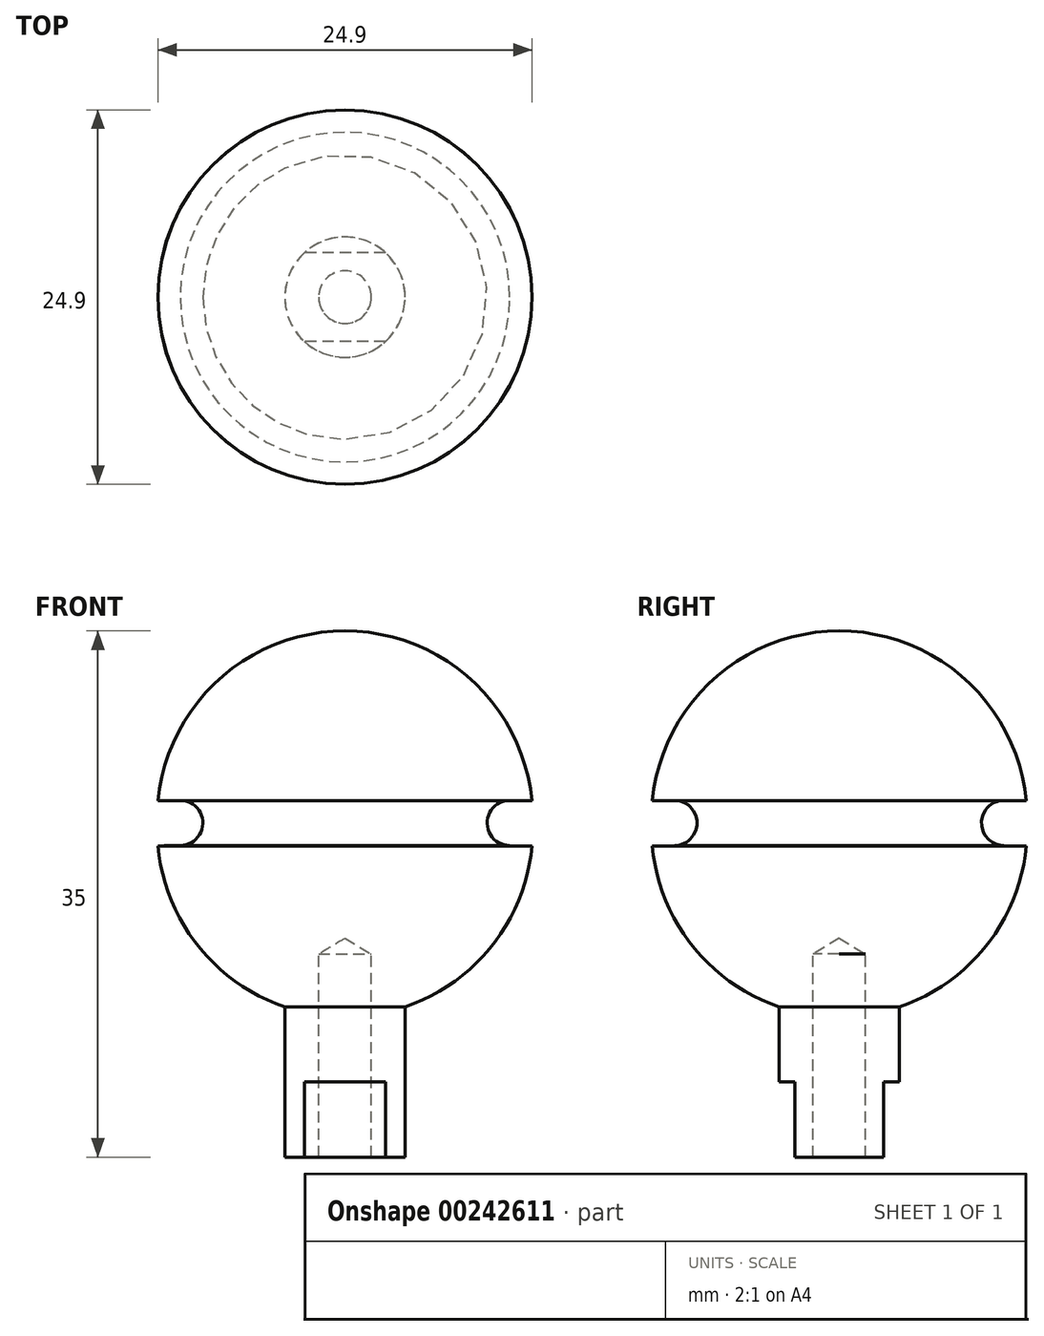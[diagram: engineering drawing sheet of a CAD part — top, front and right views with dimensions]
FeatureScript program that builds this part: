
annotation { "Feature Type Name" : "Feature", "Feature Type Description" : "" }
export const myFeature = defineFeature(function(context is Context, id is Id, definition is map)
    precondition{}
    {
        {
            var Q0;
            Q0=qCreatedBy(makeId("Top.planeOp"),FACE);
            var sketch = newSketch(context, id + "F0", { "sketchPlane" : qUnion([Q0])});
            skPoint(sketch, "E0", {"position": v(0, 0) * mm});
            skCircle(sketch, "E1", {"center": v(0, 0) * mm, "radius": 4 * mm});
            skSolve(sketch);
        }
        {
            var Q0;
            Q0=makeQuery(id+"F0.imprint","IMPRINT",FACE,{"disambiguationData":[TD([[makeQuery(id+"F0.imprint","IMPRINT",EDGE,{"derivedFrom":sQuery(id+"F0.wireOp",EDGE,"E1")}),1.0]])]});
            extrude(context, id + "F1", {"entities" : qUnion([Q0]), "offsetDistance" : 25 * mm, "depth" : 10 * mm});
        }
        {
            var Q0;
            Q0=makeQuery(id+"F1.opExtrude","CAP_FACE",FACE,{"disambiguationData":[OSD([sQuery(id+"F0.wireOp",EDGE,"E1")])],"isStart":false});
            var sketch = newSketch(context, id + "F2", { "sketchPlane" : qUnion([Q0])});
            skCircle(sketch, "E2", {"center": v(0, 0) * mm, "radius": 12.5 * mm});
            skSolve(sketch);
        }
        {
            var Q0;
            Q0 = qSketchRegion(id + "F2", true);
            extrude(context, id + "F3", {"entities" : qUnion([Q0]), "operationType" : NewBodyOperationType.ADD, "depth" : 25 * mm, "offsetDistance" : 25 * mm});
        }
        {
            var Q0;
            Q0=makeQuery(id+"F3.opExtrude","CAP_EDGE",EDGE,{"disambiguationData":[OSD([sQuery(id+"F2.wireOp",EDGE,"E2")])],"isStart":false});
            var Q1;
            Q1=makeQuery(id+"F3.opExtrude","CAP_EDGE",EDGE,{"disambiguationData":[OSD([sQuery(id+"F2.wireOp",EDGE,"E2")])],"isStart":true});
            fillet(context, id + "F4", {"entities" : qUnion([Q0, Q1]), "radius" : 12.5 * mm, "tangentPropagation" : true, "allowEdgeOverflow" : false});
        }
        {
            var Q0;
            Q0=qCreatedBy(makeId("Right.planeOp"),FACE);
            var sketch = newSketch(context, id + "F5", { "sketchPlane" : qUnion([Q0])});
            skLineSegment(sketch, "E3", {"start": v(12.5, 23.7) * mm, "end": v(12.5, 20.7) * mm, "construction": true});
            skPoint(sketch, "E4", {"position": v(12.5, 22.2) * mm});
            skLineSegment(sketch, "E5", {"start": v(10.96, 23.73) * mm, "end": v(10.96, 20.73) * mm, "construction": true});
            skPoint(sketch, "E6", {"position": v(10.96, 22.23) * mm});
            skArc(sketch, "E7", {"start": v(10.96, 23.73) * mm, "mid": v(9.46, 22.23) * mm, "end": v(10.96, 20.73) * mm});
            skLineSegment(sketch, "E8", {"start": v(10.96, 23.73) * mm, "end": v(12.5, 23.7) * mm});
            skLineSegment(sketch, "E9", {"start": v(12.5, 23.7) * mm, "end": v(12.5, 20.7) * mm});
            skLineSegment(sketch, "E10", {"start": v(12.5, 20.7) * mm, "end": v(10.96, 20.73) * mm});
            skSolve(sketch);
        }
        {
            var Q0;
            Q0 = qSketchRegion(id + "F5", true);
            var Q1;
            Q1=makeQuery(id+"F3.opExtrude","SWEPT_FACE",FACE,{"disambiguationData":[OSD([sQuery(id+"F2.wireOp",EDGE,"E2")])]});
            revolve(context, id + "F6", {"operationType" : NewBodyOperationType.REMOVE, "surfaceOperationType" : NewSurfaceOperationType.NEW, "entities" : qUnion([Q0]), "axis" : qUnion([Q1]), "revolveType" : RevolveType.FULL, "oppositeDirection" : true});
        }
        {
            var Q0;
            Q0=makeQuery(id+"F1.opExtrude","CAP_FACE",FACE,{"disambiguationData":[OSD([sQuery(id+"F0.wireOp",EDGE,"E1")])],"isStart":true});
            var sketch = newSketch(context, id + "F7", { "sketchPlane" : qUnion([Q0])});
            skLineSegment(sketch, "E11", {"start": v(-4, 0) * mm, "end": v(4, 0) * mm, "construction": true});
            skPoint(sketch, "E12", {"position": v(0, 0) * mm});
            skLineSegment(sketch, "E13", {"start": v(2.7, -2.95) * mm, "end": v(-2.7, -2.95) * mm, "construction": true});
            skLineSegment(sketch, "E14", {"start": v(2.7, 2.95) * mm, "end": v(-2.7, 2.95) * mm, "construction": true});
            skLineSegment(sketch, "E15", {"start": v(2.7, -2.95) * mm, "end": v(-2.7, -2.95) * mm});
            skLineSegment(sketch, "E16", {"start": v(2.7, 2.95) * mm, "end": v(-2.7, 2.95) * mm});
            skArc(sketch, "E17", {"start": v(2.7, 2.95) * mm, "mid": v(0, 4) * mm, "end": v(-2.7, 2.95) * mm});
            skArc(sketch, "E18", {"start": v(2.7, -2.95) * mm, "mid": v(0, -4) * mm, "end": v(-2.7, -2.95) * mm});
            skSolve(sketch);
        }
        {
            var Q0;
            Q0=makeQuery(id+"F1.opExtrude","CAP_FACE",FACE,{"disambiguationData":[OSD([sQuery(id+"F0.wireOp",EDGE,"E1")])],"isStart":true});
            var sketch = newSketch(context, id + "F8", { "sketchPlane" : qUnion([Q0])});
            skPoint(sketch, "E19", {"position": v(0, 0) * mm});
            skSolve(sketch);
        }
        {
            var Q0;
            Q0=sQuery(id+"F8.wireOp",VERTEX,"E19");
            var Q1;
            Q1=makeQuery(id+"F1.opExtrude","SWEPT_BODY",BODY,{"disambiguationData":[OSD([sQuery(id+"F0.wireOp",EDGE,"E1")])]});
            hole(context, id + "F9", {"style" : HoleStyle.SIMPLE, "endStyle" : HoleEndStyle.BLIND, "standardTappedOrClearance" : lookupTablePath({ "standard" : "ISO", "engagement" : "75%", "pitch" : "0.5 mm", "size" : "M4", "type" : "Tapped" }), "standardBlindInLast" : lookupTablePath({ "standard" : "ISO", "fit" : "Normal", "engagement" : "75%", "pitch" : "0.5 mm", "size" : "M4", "type" : "Clearance & tapped" }), "holeDiameter" : 3.5 * mm, "majorDiameter" : 4 * mm, "showTappedDepth" : true, "holeDepth" : 13.5 * mm, "isTappedThrough" : true, "tappedDepth" : 12 * mm, "tapClearance" : 3, "locations" : qUnion([Q0]), "scope" : qUnion([Q1]), "startStyle" : HoleStartStyle.SKETCH});
        }
        {
            var Q0;
            Q0 = qSketchRegion(id + "F7", true);
            extrude(context, id + "F10", {"entities" : qUnion([Q0]), "operationType" : NewBodyOperationType.REMOVE, "oppositeDirection" : true, "depth" : 5 * mm, "offsetDistance" : 25 * mm});
        }
    });
